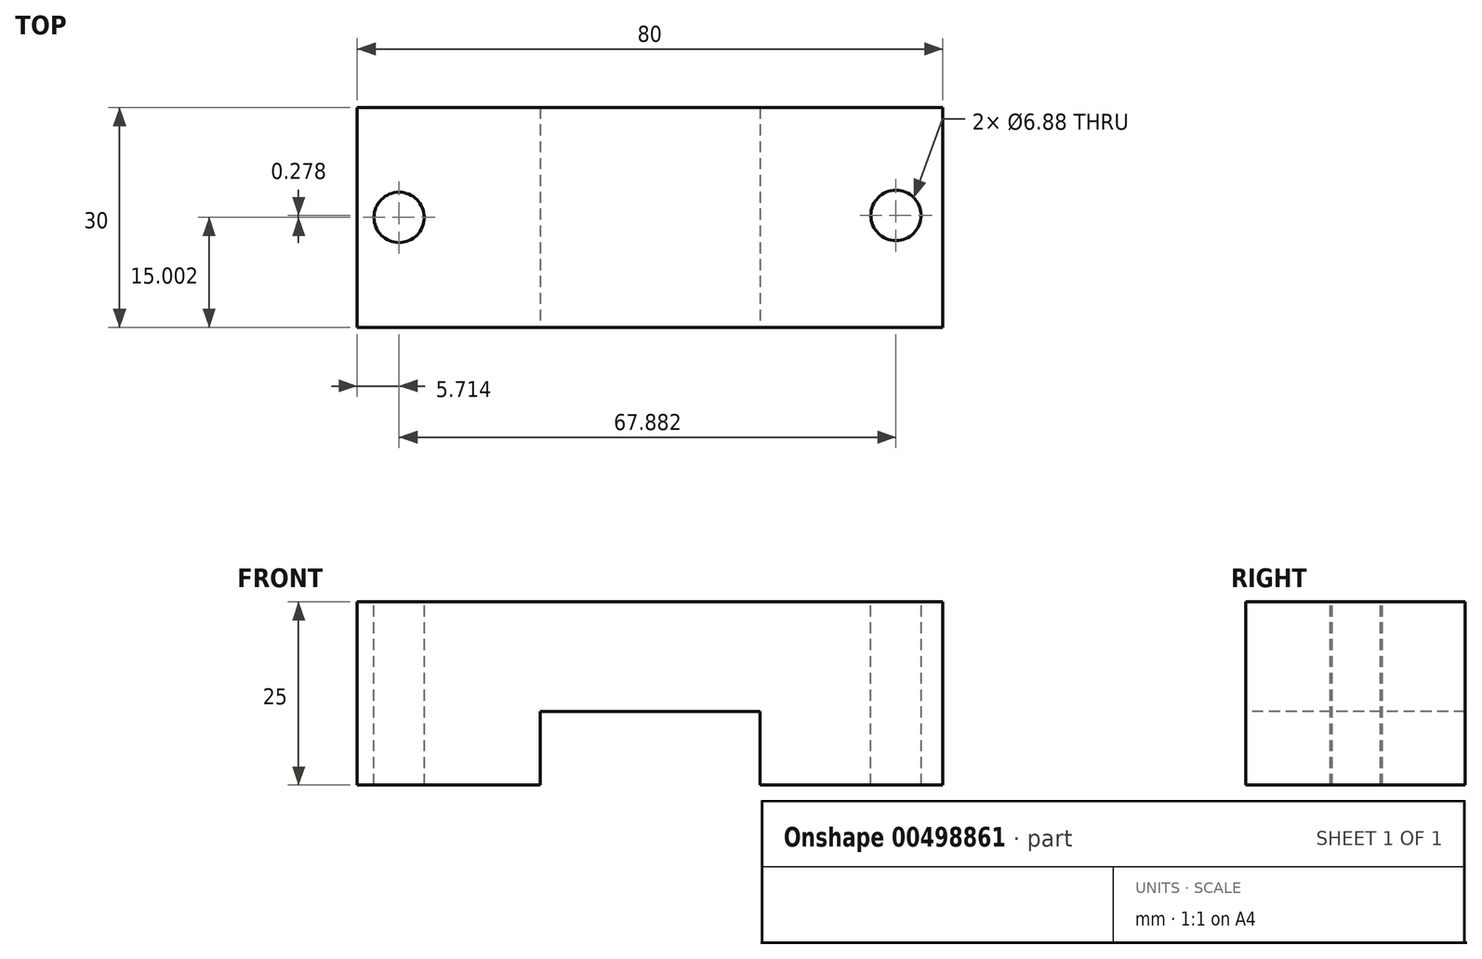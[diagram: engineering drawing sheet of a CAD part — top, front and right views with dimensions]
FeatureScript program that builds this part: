
annotation { "Feature Type Name" : "Feature", "Feature Type Description" : "" }
export const myFeature = defineFeature(function(context is Context, id is Id, definition is map)
    precondition{}
    {
        {
            var Q0;
            Q0=qCreatedBy(makeId("Top.planeOp"),FACE);
            var sketch = newSketch(context, id + "F0", { "sketchPlane" : qUnion([Q0])});
            skLineSegment(sketch, "E0.bottom", {"start": v(-68.1, 24) * mm, "end": v(11.9, 24) * mm});
            skLineSegment(sketch, "E0.top", {"start": v(-68.1, -6) * mm, "end": v(11.9, -6) * mm});
            skLineSegment(sketch, "E0.left", {"start": v(-68.1, 24) * mm, "end": v(-68.1, -6) * mm});
            skLineSegment(sketch, "E0.right", {"start": v(11.9, 24) * mm, "end": v(11.9, -6) * mm});
            skSolve(sketch);
        }
        {
            var Q0;
            Q0=makeQuery(id+"F0.imprint","IMPRINT",FACE,{"disambiguationData":[TD([[makeQuery(id+"F0.imprint","IMPRINT",EDGE,{"derivedFrom":sQuery(id+"F0.wireOp",EDGE,"E0.bottom")}),-1.0]])]});
            extrude(context, id + "F1", {"entities" : qUnion([Q0]), "depth" : 25 * mm});
        }
        {
            var Q0;
            Q0=makeQuery(id+"F1.opExtrude","SWEPT_FACE",FACE,{"disambiguationData":[OSD([sQuery(id+"F0.wireOp",EDGE,"E0.top")])]});
            var sketch = newSketch(context, id + "F2", { "sketchPlane" : qUnion([Q0])});
            skLineSegment(sketch, "E1.bottom", {"start": v(-13.1, 10) * mm, "end": v(-43.1, 10) * mm});
            skLineSegment(sketch, "E1.top", {"start": v(-13.1, -10) * mm, "end": v(-43.1, -10) * mm});
            skLineSegment(sketch, "E1.left", {"start": v(-13.1, 10) * mm, "end": v(-13.1, -10) * mm});
            skLineSegment(sketch, "E1.right", {"start": v(-43.1, 10) * mm, "end": v(-43.1, -10) * mm});
            skPoint(sketch, "E1.middle", {"position": v(-28.1, 0) * mm});
            skSolve(sketch);
        }
        {
            var Q0;
            {var subQ0=sQuery(id+"F2.wireOp",EDGE,"E1.top");Q0=makeQuery(id+"F2.imprint","IMPRINT",FACE,{"disambiguationData":[TD([[makeQuery(id+"F2.imprint","IMPRINT",EDGE,{"derivedFrom":subQ0}),-1.0]])]});}
            var Q1;
            {var subQ0=sQuery(id+"F2.wireOp",EDGE,"E1.bottom");Q1=makeQuery(id+"F2.imprint","IMPRINT",FACE,{"disambiguationData":[TD([[makeQuery(id+"F2.imprint","IMPRINT",EDGE,{"derivedFrom":subQ0}),1.0]])]});}
            extrude(context, id + "F3", {"entities" : qUnion([Q0, Q1]), "operationType" : NewBodyOperationType.REMOVE, "oppositeDirection" : true, "depth" : 100 * mm});
        }
        {
            var Q0;
            Q0=makeQuery(id+"F1.opExtrude","CAP_FACE",FACE,{"disambiguationData":[OSD([sQuery(id+"F0.wireOp",EDGE,"E0.bottom"),sQuery(id+"F0.wireOp",EDGE,"E0.top"),sQuery(id+"F0.wireOp",EDGE,"E0.left"),sQuery(id+"F0.wireOp",EDGE,"E0.right")])],"isStart":false});
            var sketch = newSketch(context, id + "F4", { "sketchPlane" : qUnion([Q0])});
            skLineSegment(sketch, "E2", {"start": v(-68.1, 9) * mm, "end": v(11.9, 9) * mm});
            skCircle(sketch, "E3", {"center": v(5.5, 9.28) * mm, "radius": 3.44 * mm});
            skPoint(sketch, "E3.first.point", {"position": v(8.92, 9) * mm});
            skPoint(sketch, "E3.second.point", {"position": v(3.9, 12.33) * mm});
            skPoint(sketch, "E3.third.point", {"position": v(5.1, 5.86) * mm});
            skSolve(sketch);
        }
        {
            var Q0;
            Q0 = qSketchRegion(id + "F4", true);
            extrude(context, id + "F5", {"entities" : qUnion([Q0]), "operationType" : NewBodyOperationType.REMOVE, "oppositeDirection" : true, "depth" : 100 * mm});
        }
        {
            var Q0;
            Q0=makeQuery(id+"F1.opExtrude","CAP_FACE",FACE,{"disambiguationData":[OSD([sQuery(id+"F0.wireOp",EDGE,"E0.bottom"),sQuery(id+"F0.wireOp",EDGE,"E0.top"),sQuery(id+"F0.wireOp",EDGE,"E0.left"),sQuery(id+"F0.wireOp",EDGE,"E0.right")])],"isStart":false});
            var sketch = newSketch(context, id + "F6", { "sketchPlane" : qUnion([Q0])});
            skCircle(sketch, "E4", {"center": v(-62.39, 9) * mm, "radius": 3.44 * mm});
            skPoint(sketch, "E4.centerSnap0", {"position": v(-68.1, 9) * mm});
            skSolve(sketch);
        }
        {
            var Q0;
            Q0=makeQuery(id+"F6.imprint","IMPRINT",FACE,{"disambiguationData":[TD([[makeQuery(id+"F6.imprint","IMPRINT",EDGE,{"derivedFrom":sQuery(id+"F6.wireOp",EDGE,"E4")}),1.0]])]});
            var Q1;
            Q1=sQuery(id+"F6.wireOp",EDGE,"E4");
            extrude(context, id + "F7", {"entities" : qUnion([Q0]), "operationType" : NewBodyOperationType.REMOVE, "surfaceEntities" : qUnion([Q1]), "oppositeDirection" : true, "depth" : 100 * mm});
        }
    });
